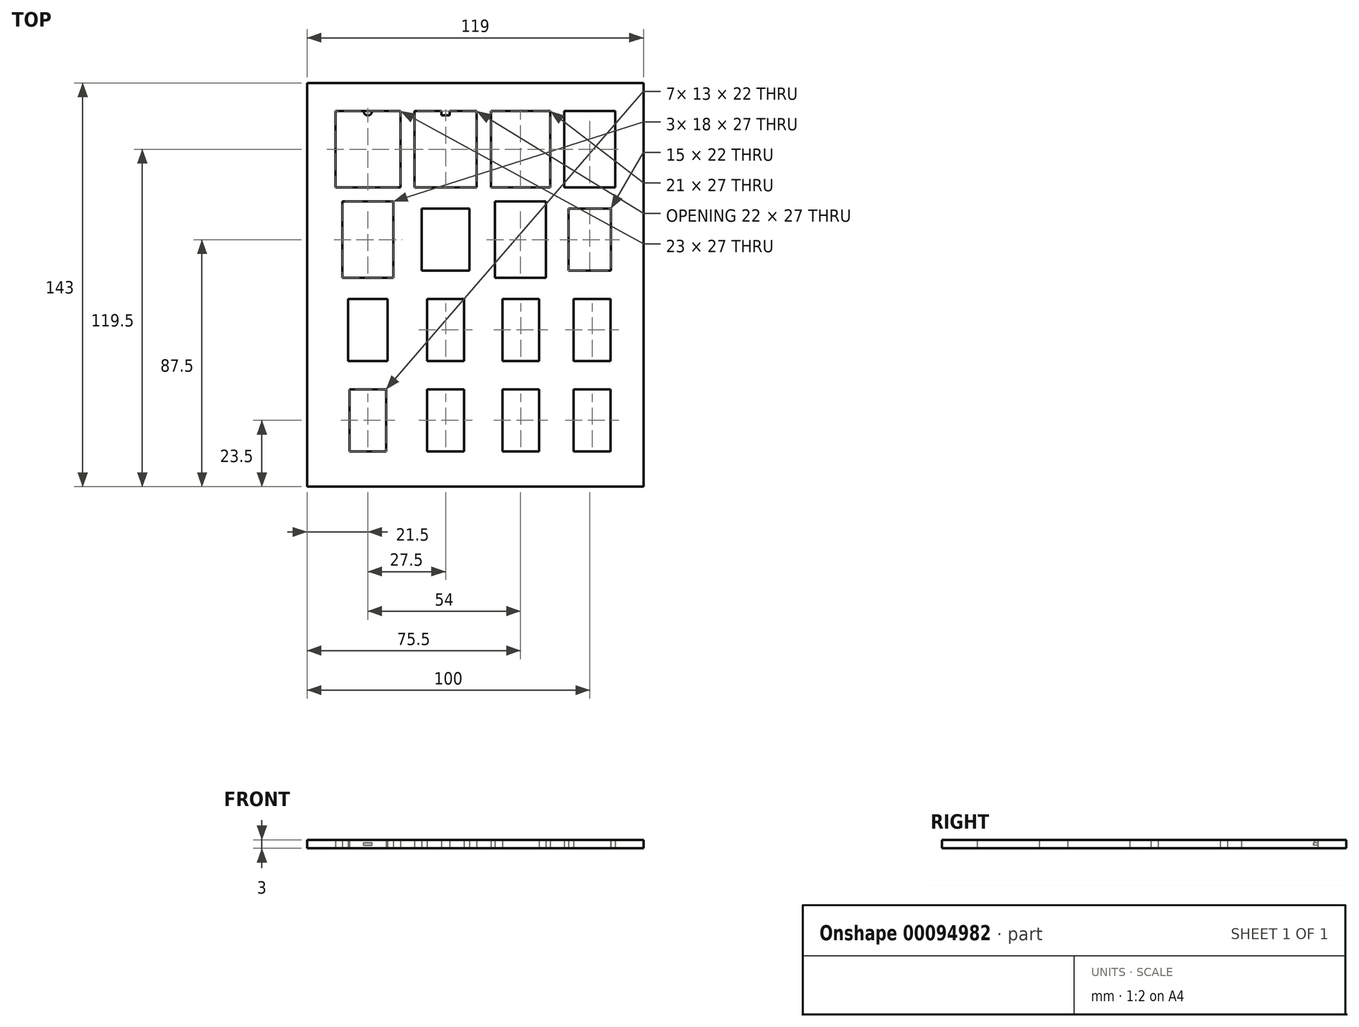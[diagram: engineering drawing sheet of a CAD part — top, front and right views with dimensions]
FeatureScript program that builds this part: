
annotation { "Feature Type Name" : "Feature", "Feature Type Description" : "" }
export const myFeature = defineFeature(function(context is Context, id is Id, definition is map)
    precondition{}
    {
        {
            var Q0;
            Q0=qCreatedBy(makeId("Top.planeOp"),FACE);
            var sketch = newSketch(context, id + "F0", { "sketchPlane" : qUnion([Q0])});
            skLineSegment(sketch, "E0.bottom", {"start": v(59.5, -71.5) * mm, "end": v(-59.5, -71.5) * mm});
            skLineSegment(sketch, "E0.top", {"start": v(59.5, 71.5) * mm, "end": v(-59.5, 71.5) * mm});
            skLineSegment(sketch, "E0.left", {"start": v(59.5, -71.5) * mm, "end": v(59.5, 71.5) * mm});
            skLineSegment(sketch, "E0.right", {"start": v(-59.5, -71.5) * mm, "end": v(-59.5, 71.5) * mm});
            skPoint(sketch, "E0.middle", {"position": v(0, 0) * mm});
            skLineSegment(sketch, "E1.bottom", {"start": v(-26.5, 34.5) * mm, "end": v(-49.5, 34.5) * mm});
            skLineSegment(sketch, "E1.top", {"start": v(-26.5, 61.5) * mm, "end": v(-49.5, 61.5) * mm});
            skLineSegment(sketch, "E1.left", {"start": v(-26.5, 34.5) * mm, "end": v(-26.5, 61.5) * mm});
            skLineSegment(sketch, "E1.right", {"start": v(-49.5, 34.5) * mm, "end": v(-49.5, 61.5) * mm});
            skPoint(sketch, "E1.middle", {"position": v(-38, 48) * mm});
            skLineSegment(sketch, "E2.bottom", {"start": v(0.5, 34.5) * mm, "end": v(-21.5, 34.5) * mm});
            skLineSegment(sketch, "E2.top", {"start": v(0.5, 61.5) * mm, "end": v(-21.5, 61.5) * mm});
            skLineSegment(sketch, "E2.left", {"start": v(0.5, 34.5) * mm, "end": v(0.5, 61.5) * mm});
            skLineSegment(sketch, "E2.right", {"start": v(-21.5, 34.5) * mm, "end": v(-21.5, 61.5) * mm});
            skPoint(sketch, "E2.middle", {"position": v(-10.5, 48) * mm});
            skLineSegment(sketch, "E3.bottom", {"start": v(5.5, 61.5) * mm, "end": v(26.5, 61.5) * mm});
            skLineSegment(sketch, "E3.top", {"start": v(5.5, 34.5) * mm, "end": v(26.5, 34.5) * mm});
            skLineSegment(sketch, "E3.left", {"start": v(5.5, 61.5) * mm, "end": v(5.5, 34.5) * mm});
            skLineSegment(sketch, "E3.right", {"start": v(26.5, 61.5) * mm, "end": v(26.5, 34.5) * mm});
            skLineSegment(sketch, "E4.bottom", {"start": v(31.5, 61.5) * mm, "end": v(49.5, 61.5) * mm});
            skLineSegment(sketch, "E4.top", {"start": v(31.5, 34.5) * mm, "end": v(49.5, 34.5) * mm});
            skLineSegment(sketch, "E4.left", {"start": v(31.5, 61.5) * mm, "end": v(31.5, 34.5) * mm});
            skLineSegment(sketch, "E4.right", {"start": v(49.5, 61.5) * mm, "end": v(49.5, 34.5) * mm});
            skLineSegment(sketch, "E5.bottom", {"start": v(33, 27) * mm, "end": v(48, 27) * mm});
            skLineSegment(sketch, "E5.top", {"start": v(33, 5) * mm, "end": v(48, 5) * mm});
            skLineSegment(sketch, "E5.left", {"start": v(33, 27) * mm, "end": v(33, 5) * mm});
            skLineSegment(sketch, "E5.right", {"start": v(48, 27) * mm, "end": v(48, 5) * mm});
            skPoint(sketch, "E6", {"position": v(40.5, 48) * mm});
            skPoint(sketch, "E6.positionSnap0", {"position": v(40.5, 34.5) * mm});
            skPoint(sketch, "E6.positionSnap1", {"position": v(49.5, 48) * mm});
            skPoint(sketch, "E7", {"position": v(16, 48) * mm});
            skPoint(sketch, "E7.positionSnap0", {"position": v(16, 34.5) * mm});
            skPoint(sketch, "E8", {"position": v(40.5, 16) * mm});
            skPoint(sketch, "E8.positionSnap0", {"position": v(40.5, 5) * mm});
            skPoint(sketch, "E8.positionSnap1", {"position": v(48, 16) * mm});
            skLineSegment(sketch, "E9.bottom", {"start": v(-19, 27) * mm, "end": v(-2, 27) * mm});
            skLineSegment(sketch, "E9.top", {"start": v(-19, 5) * mm, "end": v(-2, 5) * mm});
            skLineSegment(sketch, "E9.left", {"start": v(-19, 27) * mm, "end": v(-19, 5) * mm});
            skLineSegment(sketch, "E9.right", {"start": v(-2, 27) * mm, "end": v(-2, 5) * mm});
            skPoint(sketch, "E10", {"position": v(-10.5, 16) * mm});
            skPoint(sketch, "E10.positionSnap0", {"position": v(-2, 16) * mm});
            skPoint(sketch, "E10.positionSnap1", {"position": v(-10.5, 5) * mm});
            skLineSegment(sketch, "E11.bottom", {"start": v(-47, 29.5) * mm, "end": v(-29, 29.5) * mm});
            skLineSegment(sketch, "E11.top", {"start": v(-47, 2.5) * mm, "end": v(-29, 2.5) * mm});
            skLineSegment(sketch, "E11.left", {"start": v(-47, 29.5) * mm, "end": v(-47, 2.5) * mm});
            skLineSegment(sketch, "E11.right", {"start": v(-29, 29.5) * mm, "end": v(-29, 2.5) * mm});
            skPoint(sketch, "E12", {"position": v(-38, 16) * mm});
            skPoint(sketch, "E12.positionSnap0", {"position": v(-29, 16) * mm});
            skPoint(sketch, "E12.positionSnap1", {"position": v(-38, 2.5) * mm});
            skLineSegment(sketch, "E13.bottom", {"start": v(7, 29.5) * mm, "end": v(25, 29.5) * mm});
            skLineSegment(sketch, "E13.top", {"start": v(7, 2.5) * mm, "end": v(25, 2.5) * mm});
            skLineSegment(sketch, "E13.left", {"start": v(7, 29.5) * mm, "end": v(7, 2.5) * mm});
            skLineSegment(sketch, "E13.right", {"start": v(25, 29.5) * mm, "end": v(25, 2.5) * mm});
            skPoint(sketch, "E14", {"position": v(16, 16) * mm});
            skPoint(sketch, "E14.positionSnap0", {"position": v(25, 16) * mm});
            skPoint(sketch, "E14.positionSnap1", {"position": v(16, 2.5) * mm});
            skLineSegment(sketch, "E15.bottom", {"start": v(-45, -5) * mm, "end": v(-31, -5) * mm});
            skLineSegment(sketch, "E15.top", {"start": v(-45, -27) * mm, "end": v(-31, -27) * mm});
            skLineSegment(sketch, "E15.left", {"start": v(-45, -5) * mm, "end": v(-45, -27) * mm});
            skLineSegment(sketch, "E15.right", {"start": v(-31, -5) * mm, "end": v(-31, -27) * mm});
            skLineSegment(sketch, "E16.bottom", {"start": v(9.58, -5) * mm, "end": v(22.58, -5) * mm});
            skLineSegment(sketch, "E16.top", {"start": v(9.58, -27) * mm, "end": v(22.58, -27) * mm});
            skLineSegment(sketch, "E16.left", {"start": v(9.58, -5) * mm, "end": v(9.58, -27) * mm});
            skLineSegment(sketch, "E16.right", {"start": v(22.58, -5) * mm, "end": v(22.58, -27) * mm});
            skPoint(sketch, "E17.firstSnap0", {"position": v(16.08, -5) * mm});
            skLineSegment(sketch, "E17.bottom", {"start": v(34.82, -5) * mm, "end": v(47.82, -5) * mm});
            skLineSegment(sketch, "E17.top", {"start": v(34.82, -27) * mm, "end": v(47.82, -27) * mm});
            skLineSegment(sketch, "E17.left", {"start": v(34.82, -5) * mm, "end": v(34.82, -27) * mm});
            skLineSegment(sketch, "E17.right", {"start": v(47.82, -5) * mm, "end": v(47.82, -27) * mm});
            skPoint(sketch, "E18", {"position": v(-38, -16) * mm});
            skPoint(sketch, "E18.positionSnap0", {"position": v(-31, -16) * mm});
            skPoint(sketch, "E18.positionSnap1", {"position": v(-38, -27) * mm});
            skPoint(sketch, "E19", {"position": v(16.08, -16) * mm});
            skPoint(sketch, "E19.positionSnap0", {"position": v(22.58, -16) * mm});
            skPoint(sketch, "E19.positionSnap1", {"position": v(16.08, -27) * mm});
            skPoint(sketch, "E20", {"position": v(41.32, -16) * mm});
            skPoint(sketch, "E20.positionSnap0", {"position": v(47.82, -16) * mm});
            skPoint(sketch, "E20.positionSnap1", {"position": v(41.32, -27) * mm});
            skLineSegment(sketch, "E21.bottom", {"start": v(-17, -5) * mm, "end": v(-4, -5) * mm});
            skLineSegment(sketch, "E21.top", {"start": v(-17, -27) * mm, "end": v(-4, -27) * mm});
            skLineSegment(sketch, "E21.left", {"start": v(-17, -5) * mm, "end": v(-17, -27) * mm});
            skLineSegment(sketch, "E21.right", {"start": v(-4, -5) * mm, "end": v(-4, -27) * mm});
            skPoint(sketch, "E22", {"position": v(-10.5, -16) * mm});
            skPoint(sketch, "E22.positionSnap0", {"position": v(-4, -16) * mm});
            skPoint(sketch, "E22.positionSnap1", {"position": v(-10.5, -27) * mm});
            skLineSegment(sketch, "E23.bottom", {"start": v(-44.5, -37) * mm, "end": v(-31.5, -37) * mm});
            skLineSegment(sketch, "E23.top", {"start": v(-44.5, -59) * mm, "end": v(-31.5, -59) * mm});
            skLineSegment(sketch, "E23.left", {"start": v(-44.5, -37) * mm, "end": v(-44.5, -59) * mm});
            skLineSegment(sketch, "E23.right", {"start": v(-31.5, -37) * mm, "end": v(-31.5, -59) * mm});
            skLineSegment(sketch, "E24.bottom", {"start": v(-17, -37) * mm, "end": v(-4, -37) * mm});
            skLineSegment(sketch, "E24.top", {"start": v(-17, -59) * mm, "end": v(-4, -59) * mm});
            skLineSegment(sketch, "E24.left", {"start": v(-17, -37) * mm, "end": v(-17, -59) * mm});
            skLineSegment(sketch, "E24.right", {"start": v(-4, -37) * mm, "end": v(-4, -59) * mm});
            skLineSegment(sketch, "E25.bottom", {"start": v(9.58, -37) * mm, "end": v(22.58, -37) * mm});
            skLineSegment(sketch, "E25.top", {"start": v(9.58, -59) * mm, "end": v(22.58, -59) * mm});
            skLineSegment(sketch, "E25.left", {"start": v(9.58, -37) * mm, "end": v(9.58, -59) * mm});
            skLineSegment(sketch, "E25.right", {"start": v(22.58, -37) * mm, "end": v(22.58, -59) * mm});
            skLineSegment(sketch, "E26.bottom", {"start": v(34.82, -37) * mm, "end": v(47.82, -37) * mm});
            skLineSegment(sketch, "E26.top", {"start": v(34.82, -59) * mm, "end": v(47.82, -59) * mm});
            skLineSegment(sketch, "E26.left", {"start": v(34.82, -37) * mm, "end": v(34.82, -59) * mm});
            skLineSegment(sketch, "E26.right", {"start": v(47.82, -37) * mm, "end": v(47.82, -59) * mm});
            skPoint(sketch, "E27", {"position": v(-38, -48) * mm});
            skPoint(sketch, "E27.positionSnap0", {"position": v(-31.5, -48) * mm});
            skPoint(sketch, "E27.positionSnap1", {"position": v(-38, -59) * mm});
            skPoint(sketch, "E28", {"position": v(-10.5, -48) * mm});
            skPoint(sketch, "E28.positionSnap0", {"position": v(-10.5, -59) * mm});
            skPoint(sketch, "E28.positionSnap1", {"position": v(-4, -48) * mm});
            skPoint(sketch, "E29", {"position": v(16.08, -48) * mm});
            skPoint(sketch, "E29.positionSnap0", {"position": v(22.58, -48) * mm});
            skPoint(sketch, "E29.positionSnap1", {"position": v(16.08, -59) * mm});
            skPoint(sketch, "E30", {"position": v(41.32, -48) * mm});
            skPoint(sketch, "E30.positionSnap0", {"position": v(47.82, -48) * mm});
            skPoint(sketch, "E30.positionSnap1", {"position": v(41.32, -59) * mm});
            skPoint(sketch, "E31", {"position": v(-44.5, -49.5) * mm});
            skPoint(sketch, "E32", {"position": v(-17, -48.5) * mm});
            skPoint(sketch, "E33", {"position": v(9.58, -48.5) * mm});
            skPoint(sketch, "E34", {"position": v(34.82, -48.5) * mm});
            skLineSegment(sketch, "E35", {"start": v(-42.75, -50.27) * mm, "end": v(-33.25, -50.27) * mm});
            skPoint(sketch, "E36", {"position": v(-38, -50.27) * mm});
            skLineSegment(sketch, "E37", {"start": v(-15.25, -51.11) * mm, "end": v(-5.75, -51.11) * mm});
            skPoint(sketch, "E38", {"position": v(-10.5, -51.11) * mm});
            skLineSegment(sketch, "E39", {"start": v(11.58, -50.9) * mm, "end": v(20.58, -50.9) * mm});
            skPoint(sketch, "E40", {"position": v(16.08, -50.9) * mm});
            skLineSegment(sketch, "E41", {"start": v(36.82, -50.7) * mm, "end": v(45.82, -50.7) * mm});
            skPoint(sketch, "E42", {"position": v(41.32, -50.7) * mm});
            skSolve(sketch);
        }
        {
            var Q0;
            Q0=makeQuery(id+"F0.imprint","IMPRINT",FACE,{"disambiguationData":[TD([[makeQuery(id+"F0.imprint","IMPRINT",EDGE,{"derivedFrom":sQuery(id+"F0.wireOp",EDGE,"E0.bottom")}),-1.0]])]});
            extrude(context, id + "F1", {"entities" : qUnion([Q0]), "depth" : 3 * mm});
        }
        {
            var Q0;
            Q0=makeQuery(id+"F1.opExtrude","SWEPT_FACE",FACE,{"disambiguationData":[OSD([sQuery(id+"F0.wireOp",EDGE,"E1.top")])]});
            var sketch = newSketch(context, id + "F2", { "sketchPlane" : qUnion([Q0])});
            skLineSegment(sketch, "E43", {"start": v(-49.5, 3) * mm, "end": v(-26.5, 3) * mm});
            skPoint(sketch, "E44", {"position": v(-38, 3) * mm});
            skLineSegment(sketch, "E45", {"start": v(-38, 3) * mm, "end": v(-38, 0) * mm});
            skPoint(sketch, "E46", {"position": v(-38, 1.5) * mm});
            skLineSegment(sketch, "E47.bottom", {"start": v(-38, 2) * mm, "end": v(-36.5, 2) * mm});
            skLineSegment(sketch, "E47.top", {"start": v(-38, 1) * mm, "end": v(-36.5, 1) * mm});
            skLineSegment(sketch, "E47.left", {"start": v(-38, 2) * mm, "end": v(-38, 1) * mm});
            skLineSegment(sketch, "E47.right", {"start": v(-36.5, 2) * mm, "end": v(-36.5, 1) * mm});
            skSolve(sketch);
        }
        {
            var Q0;
            Q0=makeQuery(id+"F2.imprint","IMPRINT",FACE,{"disambiguationData":[TD([[makeQuery(id+"F2.imprint","IMPRINT",EDGE,{"derivedFrom":sQuery(id+"F2.wireOp",EDGE,"E47.bottom")}),-1.0]])]});
            var Q1;
            Q1=sQuery(id+"F2.wireOp",EDGE,"E45");
            revolve(context, id + "F3", {"operationType" : NewBodyOperationType.ADD, "entities" : qUnion([Q0]), "axis" : qUnion([Q1]), "revolveType" : RevolveType.FULL});
        }
        {
            var Q0;
            Q0=makeQuery(id+"F1.opExtrude","SWEPT_FACE",FACE,{"disambiguationData":[OSD([sQuery(id+"F0.wireOp",EDGE,"E2.top")])]});
            var sketch = newSketch(context, id + "F4", { "sketchPlane" : qUnion([Q0])});
            skLineSegment(sketch, "E48", {"start": v(-10.5, 3) * mm, "end": v(-10.5, 0) * mm});
            skPoint(sketch, "E49", {"position": v(-10.5, 1.5) * mm});
            skPoint(sketch, "E50", {"position": v(0.5, 1.5) * mm});
            skLineSegment(sketch, "E51", {"start": v(0.5, 1.5) * mm, "end": v(-21.5, 1.5) * mm});
            skLineSegment(sketch, "E52", {"start": v(-10.5, 3) * mm, "end": v(-10.5, 1.5) * mm});
            skPoint(sketch, "E53", {"position": v(-10.5, 2.25) * mm});
            skLineSegment(sketch, "E54.bottom", {"start": v(-9.04, 3) * mm, "end": v(-11.96, 3) * mm});
            skLineSegment(sketch, "E54.top", {"start": v(-9.04, 1.5) * mm, "end": v(-11.96, 1.5) * mm});
            skLineSegment(sketch, "E54.left", {"start": v(-9.04, 3) * mm, "end": v(-9.04, 1.5) * mm});
            skLineSegment(sketch, "E54.right", {"start": v(-11.96, 3) * mm, "end": v(-11.96, 1.5) * mm});
            skSolve(sketch);
        }
        {
            var Q0;
            {var subQ5=sQuery(id+"F4.wireOp",EDGE,"E54.right");Q0=makeQuery(id+"F4.imprint","IMPRINT",FACE,{"disambiguationData":[TD([[makeQuery(id+"F4.imprint","IMPRINT",EDGE,{"derivedFrom":subQ5}),1.0]])]});}
            var Q1;
            {var subQ5=sQuery(id+"F4.wireOp",EDGE,"E54.left");Q1=makeQuery(id+"F4.imprint","IMPRINT",FACE,{"disambiguationData":[TD([[makeQuery(id+"F4.imprint","IMPRINT",EDGE,{"derivedFrom":subQ5}),-1.0]])]});}
            var Q2;
            Q2=sQuery(id+"F4.wireOp",EDGE,"E51");
            revolve(context, id + "F5", {"operationType" : NewBodyOperationType.ADD, "entities" : qUnion([Q0, Q1]), "axis" : qUnion([Q2]), "revolveType" : RevolveType.FULL});
        }
    });
